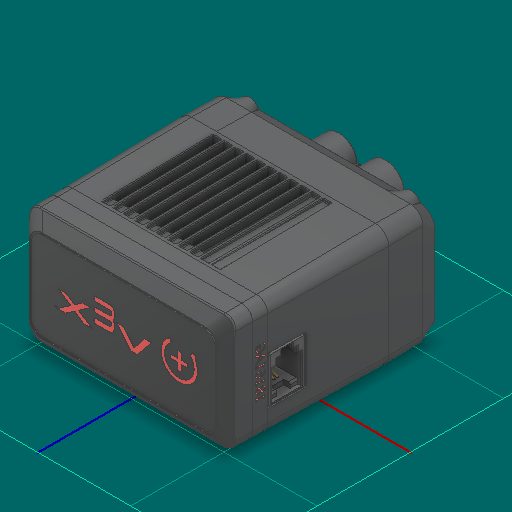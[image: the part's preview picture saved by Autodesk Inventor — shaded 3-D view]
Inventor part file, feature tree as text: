
AUTODESK INVENTOR PART (.ipt)
format: ipt  version: 2025 (Build 290162000, 162)  size: 13,132,288 bytes
history: native  units: in
note: dims shown in document units (in); Inventor stores cm internally (conversion verified against a paired STEP export)
features: other x19, sketch x2
ambient origin geometry x8: Origin, YZ Plane, XZ Plane, XY Plane, X Axis, Y Axis, Z Axis, Center Point
bodies: Solid1 (feature_tree), Solid2 (feature_tree), Solid7 (feature_tree), Solid8 (feature_tree), Solid9 (feature_tree), Solid20 (feature_tree), Solid21 (feature_tree), Solid22 (feature_tree)
feature tree (21):
  other  "V5 Motor.ipt"
  other  "Solid1::V5 Motor.ipt"
  other  "Solid2::V5 Motor.ipt"
  other  "Solid4::V5 Motor.ipt"
  other  "Solid6::V5 Motor.ipt"
  other  "Solid7::V5 Motor.ipt"
  other  "Solid8::V5 Motor.ipt"
  other  "Solid9::V5 Motor.ipt"
  other  "Solid14::V5 Motor.ipt"
  other  "Solid16::V5 Motor.ipt"
  other  "Solid17::V5 Motor.ipt"
  other  "Solid18::V5 Motor.ipt"
  other  "Solid19::V5 Motor.ipt"
  other  "Solid20::V5 Motor.ipt"
  other  "Solid21::V5 Motor.ipt"
  other  "Solid22::V5 Motor.ipt"
  other  "TaggingFeature1"
  sketch  "Sketch1"  dims[d0=0.3937in]
  sketch  "Sketch2"  dims[d4=0.0in d5=0.0in]
  other  "iInsert:1"
  other  "iInsert:2"
